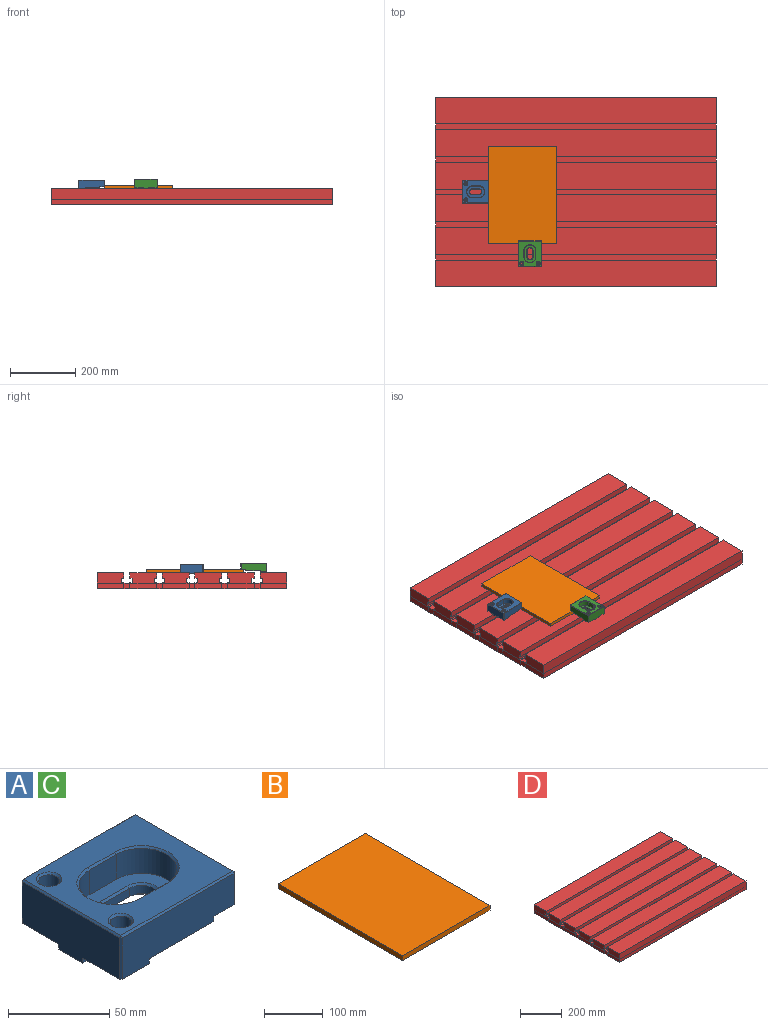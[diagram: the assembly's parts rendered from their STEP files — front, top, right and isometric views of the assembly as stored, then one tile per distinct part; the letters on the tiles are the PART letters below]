
ASSEMBLY  parts=4 mates=5
PART A: 58 faces, bbox 80x70x29 mm
  f0: plane 78x68mm, normal (0,0,1), area 3280.4mm2, adj f41,f43,f46,f47,f52,f53,f54,f55
  f1: plane 19x5mm, normal (0,-1,0), area 95mm2, adj f2,f4,f32,f33
  f2: cylinder r=8.5mm len=17mm, axis (0,0,1), area 133.5mm2, adj f1,f3,f30,f34
  f3: plane 19x5mm, normal (0,1,0), area 95mm2, adj f2,f4,f29,f36
  f4: cylinder r=8.5mm len=17mm, axis (0,0,1), area 133.5mm2, adj f1,f3,f31,f35
  f5: plane 68x28mm, normal (-1,0,0), area 1751mm2, adj f6,f14,f15,f16,f17,f39,f41,f42
  f6: plane 20x17mm, normal (0,0,-1), area 340mm2, adj f5,f7,f14,f16
  f7: plane 70x6mm, normal (1,0,0), area 261mm2, adj f6,f8,f9,f10,f14,f15,f16,f17
  f8: plane 78x25mm, normal (0,-1,0), area 1731mm2, adj f7,f10,f11,f12,f17,f39,f43,f48
  f9: plane 78x25mm, normal (0,1,0), area 1731mm2, adj f7,f10,f11,f12,f15,f42,f47,f51
  f10: plane 70x45mm, normal (0,0,-1), area 2505.5mm2, adj f7,f8,f9,f11,f29,f30,f31,f32
  f11: plane 70x3mm, normal (1,0,0), area 210mm2, adj f8,f9,f10,f12
  f12: plane 70x14mm, normal (0,0,-1), area 980mm2, adj f8,f9,f11,f50
  f13: plane 68x18mm, normal (1,0,0), area 1224mm2, adj f46,f48,f50,f51
  f14: plane 20x3mm, normal (0,1,0), area 60mm2, adj f5,f6,f7,f15
  f15: plane 26.5x20mm, normal (0,0,-1), area 479.2mm2, adj f5,f7,f9,f14,f37,f42
  f16: plane 20x3mm, normal (0,-1,0), area 60mm2, adj f5,f6,f7,f17
  f17: plane 26.5x20mm, normal (0,0,-1), area 479.2mm2, adj f5,f7,f8,f16,f38,f39
  f18: plane 54x35mm, normal (0,0,1), area 982.6mm2, adj f19,f20,f21,f22,f33,f34,f35,f36
  f19: cylinder r=17.5mm len=35mm, axis (0,0,1), area 824.7mm2, adj f18,f20,f22,f56
  f20: plane 19x15mm, normal (0,-1,0), area 285mm2, adj f18,f19,f21,f54
  f21: cylinder r=17.5mm len=35mm, axis (0,0,1), area 824.7mm2, adj f18,f20,f22,f55
  f22: plane 19x15mm, normal (0,1,0), area 285mm2, adj f18,f19,f21,f57
  f23: cylinder r=5.25mm len=19mm, axis (0,0,1), area 626.7mm2, adj f24,f52
  f24: plane 10.5x10.5mm, normal (0,0,1), area 58.3mm2, adj f23,f28
  f25: cylinder r=5.25mm len=19mm, axis (0,0,1), area 626.7mm2, adj f26,f53
  f26: plane 10.5x10.5mm, normal (0,0,1), area 58.3mm2, adj f25,f27
  f27: cylinder r=3mm len=6mm, axis (0,0,1), area 94.2mm2, adj f26,f37
  f28: cylinder r=3mm len=6mm, axis (0,0,1), area 94.2mm2, adj f24,f38
  f29: plane 19x1mm, normal (0,0.71,-0.71), area 26.9mm2, adj f3,f10,f30,f31
  f30: cone r=8.5mm half-angle=45deg, axis (0,0,-1), area 40mm2, adj f2,f10,f29,f32
  f31: cone r=8.5mm half-angle=45deg, axis (0,0,-1), area 40mm2, adj f4,f10,f29,f32
  f32: plane 19x1mm, normal (0,-0.71,-0.71), area 26.9mm2, adj f1,f10,f30,f31
  f33: plane 19x1mm, normal (0,-0.71,0.71), area 26.9mm2, adj f1,f18,f34,f35
  f34: cone r=9.5mm half-angle=45deg, axis (0,0,1), area 40mm2, adj f2,f18,f33,f36
  f35: cone r=9.5mm half-angle=45deg, axis (0,0,1), area 40mm2, adj f4,f18,f33,f36
  f36: plane 19x1mm, normal (0,0.71,0.71), area 26.9mm2, adj f3,f18,f34,f35
  f37: cone r=3mm half-angle=45deg, axis (0,0,-1), area 31.1mm2, adj f15,f27
  f38: cone r=4mm half-angle=45deg, axis (0,0,-1), area 31.1mm2, adj f17,f28
  f39: plane 25x1mm, normal (-0.71,-0.71,0), area 35.4mm2, adj f5,f8,f17,f40
  f40: plane 1x1mm, normal (-0.58,-0.58,0.58), area 0.9mm2, adj f39,f41,f43
  f41: plane 68x1mm, normal (-0.71,0,0.71), area 96.2mm2, adj f0,f5,f40,f44
  f42: plane 25x1mm, normal (-0.71,0.71,0), area 35.4mm2, adj f5,f9,f15,f44
  f43: plane 78x1mm, normal (0,-0.71,0.71), area 110.3mm2, adj f0,f8,f40,f45
  f44: plane 1x1mm, normal (-0.58,0.58,0.58), area 0.9mm2, adj f41,f42,f47
  f45: plane 1x1mm, normal (0.58,-0.58,0.58), area 0.9mm2, adj f43,f46,f48
  f46: plane 68x1mm, normal (0.71,0,0.71), area 96.2mm2, adj f0,f13,f45,f49
  f47: plane 78x1mm, normal (0,0.71,0.71), area 110.3mm2, adj f0,f9,f44,f49
  f48: plane 19x1mm, normal (0.71,-0.71,0), area 26.2mm2, adj f8,f13,f45,f50
  f49: plane 1x1mm, normal (0.58,0.58,0.58), area 0.9mm2, adj f46,f47,f51
  f50: plane 70x1mm, normal (0.71,0,-0.71), area 97.6mm2, adj f12,f13,f48,f51
  f51: plane 19x1mm, normal (0.71,0.71,0), area 26.2mm2, adj f9,f13,f49,f50
  f52: cone r=6.25mm half-angle=45deg, axis (0,0,1), area 51.1mm2, adj f0,f23
  f53: cone r=5.25mm half-angle=45deg, axis (0,0,1), area 51.1mm2, adj f0,f25
  f54: plane 19x1mm, normal (0,-0.71,0.71), area 26.9mm2, adj f0,f20,f55,f56
  f55: cone r=17.5mm half-angle=45deg, axis (0,0,1), area 80mm2, adj f0,f21,f54,f57
  f56: cone r=17.5mm half-angle=45deg, axis (0,0,1), area 80mm2, adj f0,f19,f54,f57
  f57: plane 19x1mm, normal (0,0.71,0.71), area 26.9mm2, adj f0,f22,f55,f56
PART B: 6 faces, bbox 210x300x10 mm
  f0: plane 210x10mm, normal (0,-1,0), area 2100mm2, adj f1,f3,f4,f5
  f1: plane 300x10mm, normal (1,0,0), area 3000mm2, adj f0,f2,f4,f5
  f2: plane 210x10mm, normal (0,1,0), area 2100mm2, adj f1,f3,f4,f5
  f3: plane 300x10mm, normal (-1,0,0), area 3000mm2, adj f0,f2,f4,f5
  f4: plane 300x210mm, normal (0,0,1), area 63000mm2, adj f0,f1,f2,f3
  f5: plane 300x210mm, normal (0,0,-1), area 63000mm2, adj f0,f1,f2,f3
PART C: same geometry as A
PART D: 110 faces, bbox 860x582x50 mm
  f0: plane 82x32mm, normal (1,0,0), area 2529.8mm2, adj f1,f2,f3,f4,f5,f6,f7,f8
  f1: plane 860x7.25mm, normal (0,0,1), area 6235mm2, adj f0,f2,f8,f9
  f2: plane 860x13mm, normal (0,1,0), area 11180mm2, adj f0,f1,f3,f9
  f3: plane 860x7.25mm, normal (0,0,-1), area 6235mm2, adj f0,f2,f4,f9
  f4: plane 860x18mm, normal (0,1,0), area 15480mm2, adj f0,f3,f5,f9
  f5: plane 860x82mm, normal (0,0,1), area 70520mm2, adj f0,f4,f6,f9
  f6: plane 860x32mm, normal (0,-1,0), area 27520mm2, adj f0,f5,f9,f10
  f7: plane 82x18mm, normal (1,0,0), area 1476mm2, adj f0,f10,f12,f14
  f8: plane 860x1mm, normal (0,1,0), area 860mm2, adj f0,f1,f9,f15
  f9: plane 82x32mm, normal (-1,0,0), area 2529.8mm2, adj f1,f2,f3,f4,f5,f6,f8,f16
  f10: plane 860x18mm, normal (0,-1,0), area 15480mm2, adj f6,f7,f12,f16
  f11: plane 860x1mm, normal (0,-1,0), area 860mm2, adj f13,f15,f25,f30
  f12: plane 860x82mm, normal (0,0,-1), area 70520mm2, adj f7,f10,f16,f26
  f13: plane 82x32mm, normal (1,0,0), area 2435.5mm2, adj f11,f17,f18,f19,f20,f21,f22,f23
  f14: plane 18x18mm, normal (1,0,0), area 324mm2, adj f7,f15,f26,f27
  f15: plane 860x18mm, normal (0,0,1), area 15480mm2, adj f8,f11,f14,f29
  f16: plane 82x18mm, normal (-1,0,0), area 1476mm2, adj f9,f10,f12,f29
  f17: plane 860x7.25mm, normal (0,0,1), area 6235mm2, adj f13,f18,f28,f30
  f18: plane 860x13mm, normal (0,1,0), area 11180mm2, adj f13,f17,f19,f30
  f19: plane 860x7.25mm, normal (0,0,-1), area 6235mm2, adj f13,f18,f20,f30
  f20: plane 860x18mm, normal (0,1,0), area 15480mm2, adj f13,f19,f21,f30
  f21: plane 860x82mm, normal (0,0,1), area 70520mm2, adj f13,f20,f22,f30
  f22: plane 860x18mm, normal (0,-1,0), area 15480mm2, adj f13,f21,f23,f30
  f23: plane 860x7.25mm, normal (0,0,-1), area 6235mm2, adj f13,f22,f24,f30
  f24: plane 860x13mm, normal (0,-1,0), area 11180mm2, adj f13,f23,f25,f30
  f25: plane 860x7.25mm, normal (0,0,1), area 6235mm2, adj f11,f13,f24,f30
  f26: plane 860x18mm, normal (0,0,-1), area 15480mm2, adj f12,f14,f29,f32
  f27: plane 82x18mm, normal (1,0,0), area 1476mm2, adj f13,f14,f32,f33
  f28: plane 860x1mm, normal (0,1,0), area 860mm2, adj f13,f17,f30,f35
  f29: plane 18x18mm, normal (-1,0,0), area 324mm2, adj f15,f16,f26,f36
  f30: plane 82x32mm, normal (-1,0,0), area 2435.5mm2, adj f11,f17,f18,f19,f20,f21,f22,f23
  f31: plane 860x1mm, normal (0,-1,0), area 860mm2, adj f34,f35,f45,f51
  f32: plane 860x82mm, normal (0,0,-1), area 70520mm2, adj f26,f27,f36,f46
  f33: plane 18x18mm, normal (1,0,0), area 324mm2, adj f27,f35,f46,f47
  f34: plane 82x32mm, normal (1,0,0), area 2435.5mm2, adj f31,f37,f38,f39,f40,f41,f42,f43
  f35: plane 860x18mm, normal (0,0,1), area 15480mm2, adj f28,f31,f33,f50
  f36: plane 82x18mm, normal (-1,0,0), area 1476mm2, adj f29,f30,f32,f50
  f37: plane 860x7.25mm, normal (0,0,1), area 6235mm2, adj f34,f38,f49,f51
  f38: plane 860x13mm, normal (0,1,0), area 11180mm2, adj f34,f37,f39,f51
  f39: plane 860x7.25mm, normal (0,0,-1), area 6235mm2, adj f34,f38,f40,f51
  f40: plane 860x18mm, normal (0,1,0), area 15480mm2, adj f34,f39,f41,f51
  f41: plane 860x82mm, normal (0,0,1), area 70520mm2, adj f34,f40,f42,f51
  f42: plane 860x18mm, normal (0,-1,0), area 15480mm2, adj f34,f41,f43,f51
  f43: plane 860x7.25mm, normal (0,0,-1), area 6235mm2, adj f34,f42,f44,f51
  f44: plane 860x13mm, normal (0,-1,0), area 11180mm2, adj f34,f43,f45,f51
  f45: plane 860x7.25mm, normal (0,0,1), area 6235mm2, adj f31,f34,f44,f51
  f46: plane 860x18mm, normal (0,0,-1), area 15480mm2, adj f32,f33,f50,f52
  f47: plane 82x18mm, normal (1,0,0), area 1476mm2, adj f33,f34,f52,f54
  f48: plane 860x1mm, normal (0,-1,0), area 860mm2, adj f53,f64,f65,f77
  f49: plane 860x1mm, normal (0,1,0), area 860mm2, adj f34,f37,f51,f65
  f50: plane 18x18mm, normal (-1,0,0), area 324mm2, adj f35,f36,f46,f66
  f51: plane 82x32mm, normal (-1,0,0), area 2435.5mm2, adj f31,f37,f38,f39,f40,f41,f42,f43
  f52: plane 860x82mm, normal (0,0,-1), area 70520mm2, adj f46,f47,f66,f67
  f53: plane 82x32mm, normal (1,0,0), area 2435.5mm2, adj f48,f56,f57,f58,f59,f60,f61,f62
  f54: plane 18x18mm, normal (1,0,0), area 324mm2, adj f47,f65,f67,f68
  f55: plane 82x32mm, normal (1,0,0), area 2529.8mm2, adj f69,f70,f71,f72,f73,f74,f75,f84
  f56: plane 860x7.25mm, normal (0,0,1), area 6235mm2, adj f53,f57,f76,f77
  f57: plane 860x13mm, normal (0,1,0), area 11180mm2, adj f53,f56,f58,f77
  f58: plane 860x7.25mm, normal (0,0,-1), area 6235mm2, adj f53,f57,f59,f77
  f59: plane 860x18mm, normal (0,1,0), area 15480mm2, adj f53,f58,f60,f77
  f60: plane 860x82mm, normal (0,0,1), area 70520mm2, adj f53,f59,f61,f77
  f61: plane 860x18mm, normal (0,-1,0), area 15480mm2, adj f53,f60,f62,f77
  f62: plane 860x7.25mm, normal (0,0,-1), area 6235mm2, adj f53,f61,f63,f77
  f63: plane 860x13mm, normal (0,-1,0), area 11180mm2, adj f53,f62,f64,f77
  f64: plane 860x7.25mm, normal (0,0,1), area 6235mm2, adj f48,f53,f63,f77
  f65: plane 860x18mm, normal (0,0,1), area 15480mm2, adj f48,f49,f54,f78
  f66: plane 82x18mm, normal (-1,0,0), area 1476mm2, adj f50,f51,f52,f78
  f67: plane 860x18mm, normal (0,0,-1), area 15480mm2, adj f52,f54,f78,f79
  f68: plane 82x18mm, normal (1,0,0), area 1476mm2, adj f53,f54,f79,f80
  f69: plane 860x32mm, normal (0,1,0), area 27520mm2, adj f55,f70,f82,f83
  f70: plane 860x82mm, normal (0,0,1), area 70520mm2, adj f55,f69,f71,f83
  f71: plane 860x18mm, normal (0,-1,0), area 15480mm2, adj f55,f70,f72,f83
  f72: plane 860x7.25mm, normal (0,0,-1), area 6235mm2, adj f55,f71,f73,f83
  f73: plane 860x13mm, normal (0,-1,0), area 11180mm2, adj f55,f72,f74,f83
  f74: plane 860x7.25mm, normal (0,0,1), area 6235mm2, adj f55,f73,f83,f84
  f75: plane 82x18mm, normal (1,0,0), area 1476mm2, adj f55,f81,f82,f85
  f76: plane 860x1mm, normal (0,1,0), area 860mm2, adj f53,f56,f77,f89
  f77: plane 82x32mm, normal (-1,0,0), area 2435.5mm2, adj f48,f56,f57,f58,f59,f60,f61,f62
  f78: plane 18x18mm, normal (-1,0,0), area 324mm2, adj f65,f66,f67,f90
  f79: plane 860x82mm, normal (0,0,-1), area 70520mm2, adj f67,f68,f90,f91
  f80: plane 18x18mm, normal (1,0,0), area 324mm2, adj f68,f89,f91,f92
  f81: plane 860x82mm, normal (0,0,-1), area 70520mm2, adj f75,f82,f93,f94
  f82: plane 860x18mm, normal (0,1,0), area 15480mm2, adj f69,f75,f81,f94
  f83: plane 82x32mm, normal (-1,0,0), area 2529.8mm2, adj f69,f70,f71,f72,f73,f74,f84,f94
  f84: plane 860x1mm, normal (0,-1,0), area 860mm2, adj f55,f74,f83,f95
  f85: plane 18x18mm, normal (1,0,0), area 324mm2, adj f75,f92,f93,f95
  f86: plane 860x1mm, normal (0,1,0), area 860mm2, adj f87,f95,f96,f108
  f87: plane 82x32mm, normal (1,0,0), area 2435.5mm2, adj f86,f88,f92,f96,f97,f98,f99,f100
  f88: plane 860x1mm, normal (0,-1,0), area 860mm2, adj f87,f89,f104,f108
  f89: plane 860x18mm, normal (0,0,1), area 15480mm2, adj f76,f80,f88,f105
  f90: plane 82x18mm, normal (-1,0,0), area 1476mm2, adj f77,f78,f79,f105
  f91: plane 860x18mm, normal (0,0,-1), area 15480mm2, adj f79,f80,f105,f106
  f92: plane 82x18mm, normal (1,0,0), area 1476mm2, adj f80,f85,f87,f106
  f93: plane 860x18mm, normal (0,0,-1), area 15480mm2, adj f81,f85,f106,f107
  f94: plane 82x18mm, normal (-1,0,0), area 1476mm2, adj f81,f82,f83,f107
  f95: plane 860x18mm, normal (0,0,1), area 15480mm2, adj f84,f85,f86,f107
  f96: plane 860x7.25mm, normal (0,0,1), area 6235mm2, adj f86,f87,f97,f108
  f97: plane 860x13mm, normal (0,1,0), area 11180mm2, adj f87,f96,f98,f108
  f98: plane 860x7.25mm, normal (0,0,-1), area 6235mm2, adj f87,f97,f99,f108
  f99: plane 860x18mm, normal (0,1,0), area 15480mm2, adj f87,f98,f100,f108
  f100: plane 860x82mm, normal (0,0,1), area 70520mm2, adj f87,f99,f101,f108
  f101: plane 860x18mm, normal (0,-1,0), area 15480mm2, adj f87,f100,f102,f108
  f102: plane 860x7.25mm, normal (0,0,-1), area 6235mm2, adj f87,f101,f103,f108
  f103: plane 860x13mm, normal (0,-1,0), area 11180mm2, adj f87,f102,f104,f108
  f104: plane 860x7.25mm, normal (0,0,1), area 6235mm2, adj f87,f88,f103,f108
  f105: plane 18x18mm, normal (-1,0,0), area 324mm2, adj f89,f90,f91,f109
  f106: plane 860x82mm, normal (0,0,-1), area 70520mm2, adj f91,f92,f93,f109
  f107: plane 18x18mm, normal (-1,0,0), area 324mm2, adj f93,f94,f95,f109
  f108: plane 82x32mm, normal (-1,0,0), area 2435.5mm2, adj f86,f88,f96,f97,f98,f99,f100,f101
  f109: plane 82x18mm, normal (-1,0,0), area 1476mm2, adj f105,f106,f107,f108
PLACE A t=(81.79,35.5,-3)mm
PLACE B t=(266.36,-9.42,0)mm
PLACE C rot(axis=(0,0,1),90deg) t=(253.63,-229.74,0)mm
PLACE D at identity fixed
MATE planar A.f14 <-> D.f61  axis (0,1,0) through (91.79,9,-1.5)mm
MATE planar C.f6 <-> D.f5  axis (0,0,-1) through (288.63,-219.74,0)mm
MATE planar B.f5 <-> D.f41  axis (0,0,-1) through (266.36,-9.42,0)mm
MATE planar A.f15 <-> D.f60  axis (0,0,-1) through (91.8,21.9,0)mm
MATE parallel B.f0 <-> C.f13  axis (0,-1,0) through (266.36,-159.42,5)mm
